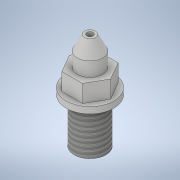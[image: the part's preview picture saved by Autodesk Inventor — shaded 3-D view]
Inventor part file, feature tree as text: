
AUTODESK INVENTOR PART (.ipt)
format: ipt  version: 2021 (Build 250183000, 183)  size: 146,944 bytes
history: native  units: mm
features: sketch x6, extrude x5, plane x1, loft x1, thread x1, other x1
ambient origin geometry x8: Origin, YZ Plane, XZ Plane, XY Plane, X Axis, Y Axis, Z Axis, Center Point
bodies: Solid1 (feature_tree)
feature tree (15):
  extrude  "Extrusion1"  Depth=4.5mm TaperAngle=0.0deg
  plane  "Work Plane1"
  loft  "Loft1"
  sketch  "Sketch3"  dims[d5=0.0mm d6=90.0deg d7=0.0mm d8=90.0deg]
  extrude  "Extrusion2"  TaperAngle=0.0deg  [1 undecoded]
  extrude  "Extrusion3"  Depth=5.5mm TaperAngle=0.0deg
  extrude  "Extrusion4"  Depth=2.0mm TaperAngle=0.0deg
  thread  "Thread1"  [1 undecoded]
  extrude  "Extrusion5"  Depth=10.0mm TaperAngle=0.0deg
  sketch  "Sketch1"  dims[d0=8.0mm d1=4.5mm d2=0.0mm]
  sketch  "Sketch2"  dims[d3=4.5mm d4=3.5mm]
  other  "Edges1"
  sketch  "Sketch4"  dims[d9=2.0mm d10=5.5mm d11=0.0mm]
  sketch  "Sketch5"  dims[d12=15.0mm d13=2.0mm d14=0.0mm d15=10.0mm]
  sketch  "Sketch6"  dims[d16=14.0mm d17=0.0mm d18=10.0mm d19=0.0mm d20=14.0mm d21=0.0mm]
note: 2 required parameter values undecoded (feature->parameter linkage not recoverable at this tier; creation-order binding heuristic only, values carry confidence <= 0.55)
